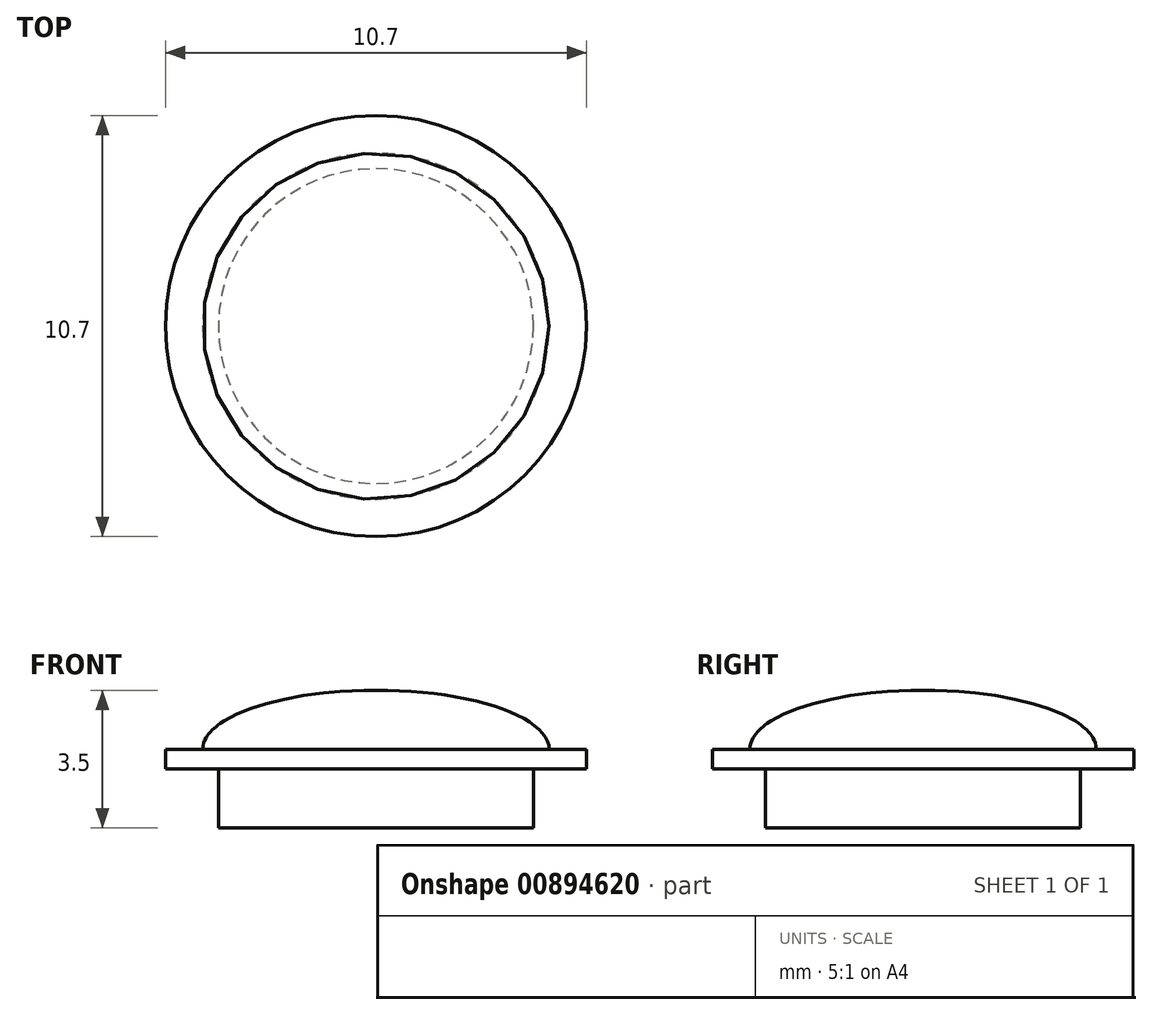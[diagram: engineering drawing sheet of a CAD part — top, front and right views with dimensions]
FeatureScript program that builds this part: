
annotation { "Feature Type Name" : "Feature", "Feature Type Description" : "" }
export const myFeature = defineFeature(function(context is Context, id is Id, definition is map)
    precondition{}
    {
        {
            var Q0;
            Q0=qCreatedBy(makeId("Front.planeOp"),FACE);
            var sketch = newSketch(context, id + "F0", { "sketchPlane" : qUnion([Q0])});
            skLineSegment(sketch, "E0", {"start": v(0, 0) * mm, "end": v(4, 0) * mm});
            skLineSegment(sketch, "E1.0", {"start": v(4, 1.5) * mm, "end": v(5.35, 1.5) * mm});
            skLineSegment(sketch, "E2", {"start": v(4, 1.5) * mm, "end": v(4, 0) * mm});
            skLineSegment(sketch, "E3", {"start": v(5.35, 1.5) * mm, "end": v(5.35, 2) * mm});
            skLineSegment(sketch, "E4.0", {"start": v(4.4, 2) * mm, "end": v(5.35, 2) * mm});
            skEllipticalArc(sketch, "E5.trimOffspring", {});
            skLineSegment(sketch, "E6", {"start": v(0, 3.5) * mm, "end": v(0, 0) * mm});
            const initialGuessF0  = {"E5.trimOffspring": [0, 0.002, 1, 0, 0.0044, 0.0015, 0, 1.5707963267948966]};
            skSetInitialGuess(sketch, initialGuessF0);
            skSolve(sketch);
        }
        {
            var Q0;
            Q0=sQuery(id+"F0.wireOp",EDGE,"E5.trimOffspring");
            var Q1;
            Q1=sQuery(id+"F0.wireOp",EDGE,"E4.0");
            var Q2;
            Q2=sQuery(id+"F0.wireOp",EDGE,"E3");
            var Q3;
            Q3=sQuery(id+"F0.wireOp",EDGE,"E1.0");
            var Q4;
            Q4=sQuery(id+"F0.wireOp",EDGE,"E2");
            var Q5;
            Q5=sQuery(id+"F0.wireOp",EDGE,"E0");
            var Q6;
            Q6=sQuery(id+"F0.wireOp",EDGE,"E6");
            revolve(context, id + "F1", {"bodyType" : ToolBodyType.SURFACE, "surfaceOperationType" : NewSurfaceOperationType.NEW, "surfaceEntities" : qUnion([Q0, Q1, Q2, Q3, Q4, Q5]), "axis" : qUnion([Q6]), "revolveType" : RevolveType.FULL});
        }
    });
